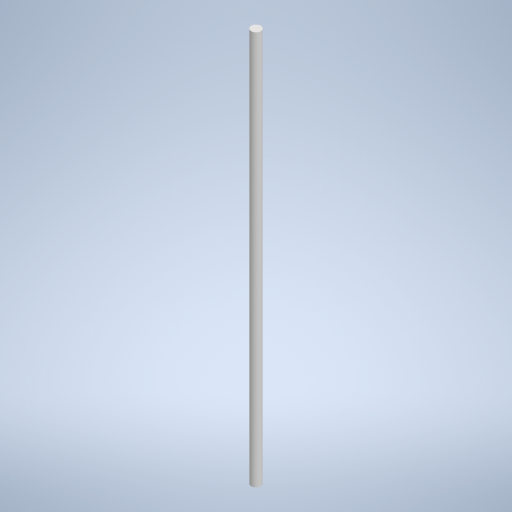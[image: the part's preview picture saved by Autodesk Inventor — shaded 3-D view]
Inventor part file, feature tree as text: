
AUTODESK INVENTOR PART (.ipt)
format: ipt  version: 2024.2 (Build 282272000, 272)  size: 235,008 bytes
history: native  units: mm
features: other x1, extrude x1, sketch x1
ambient origin geometry x8: Origin, YZ Plane, XZ Plane, XY Plane, X Axis, Y Axis, Z Axis, Center Point
bodies: Body1 (feature_tree)
feature tree (3):
  other  "Bryła1"
  extrude  "Wyciągnięcie proste1"  Depth=6.0mm
  sketch  "Szkic1"
